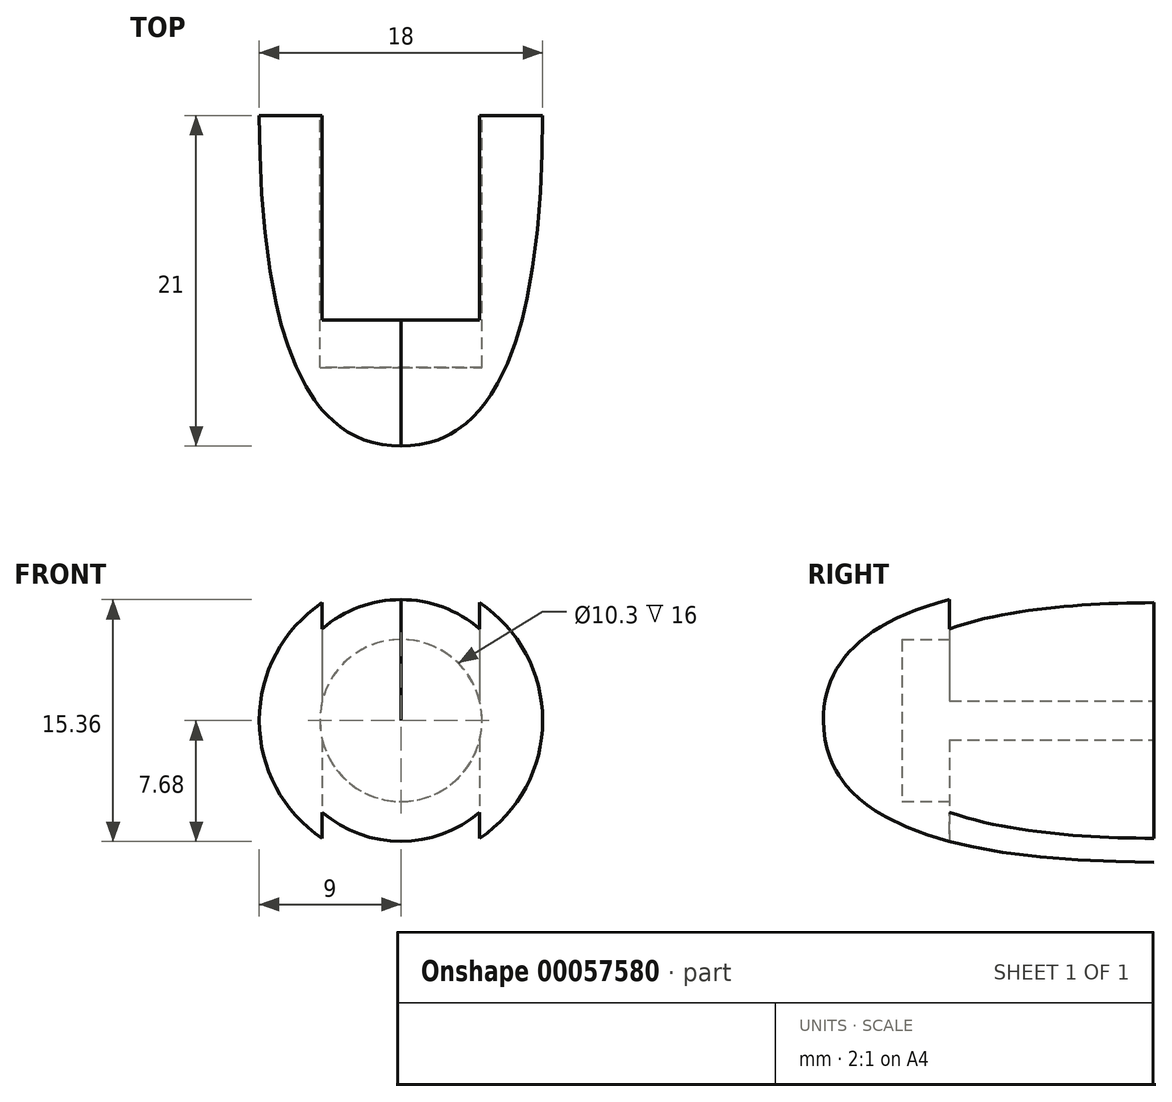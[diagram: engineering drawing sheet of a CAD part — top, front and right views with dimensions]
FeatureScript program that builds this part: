
annotation { "Feature Type Name" : "Feature", "Feature Type Description" : "" }
export const myFeature = defineFeature(function(context is Context, id is Id, definition is map)
    precondition{}
    {
        {
            var Q0;
            Q0=qCreatedBy(makeId("Right.planeOp"),FACE);
            var sketch = newSketch(context, id + "F0", { "sketchPlane" : qUnion([Q0])});
            skLineSegment(sketch, "E0", {"start": v(0, 0) * mm, "end": v(0, 5.15) * mm});
            skLineSegment(sketch, "E1", {"start": v(0, 5.15) * mm, "end": v(-16, 5.15) * mm});
            skLineSegment(sketch, "E2", {"start": v(-16, 5.15) * mm, "end": v(-16, 0) * mm});
            skLineSegment(sketch, "E3", {"start": v(-16, 0) * mm, "end": v(-21, 0) * mm});
            skFitSpline(sketch, "E4", {"points": [v(-21, 0) * mm, v(0, 9) * mm], "startDerivative": vector(0, 15.45) * mm, "endDerivative": vector(48, 0.13) * mm});
            skLineSegment(sketch, "E5", {"start": v(0, 9) * mm, "end": v(0, 5.15) * mm});
            skSolve(sketch);
        }
        {
            var Q0;
            Q0=makeQuery(id+"F0.imprint","IMPRINT",FACE,{"disambiguationData":[TD([[makeQuery(id+"F0.imprint","IMPRINT",EDGE,{"derivedFrom":sQuery(id+"F0.wireOp",EDGE,"E1")}),-1.0]])]});
            var Q1;
            Q1=sQuery(id+"F0.wireOp",EDGE,"E3");
            revolve(context, id + "F1", {"entities" : qUnion([Q0]), "axis" : qUnion([Q1]), "revolveType" : RevolveType.FULL});
        }
        {
            var Q0;
            Q0=makeQuery(id+"F1.opRevolve","SWEPT_FACE",FACE,{"disambiguationData":[OSD([sQuery(id+"F0.wireOp",EDGE,"E5")])]});
            var sketch = newSketch(context, id + "F2", { "sketchPlane" : qUnion([Q0])});
            skLineSegment(sketch, "E6.bottom", {"start": v(-5, 9) * mm, "end": v(5, 9) * mm});
            skLineSegment(sketch, "E6.left", {"start": v(-5, 9) * mm, "end": v(-5, -9) * mm});
            skLineSegment(sketch, "E6.right", {"start": v(5, 9) * mm, "end": v(5, -9) * mm});
            skLineSegment(sketch, "E7", {"start": v(-5, -9) * mm, "end": v(5, -9) * mm});
            skSolve(sketch);
        }
        {
            var Q0;
            Q0 = qSketchRegion(id + "F2", true);
            extrude(context, id + "F3", {"entities" : qUnion([Q0]), "operationType" : NewBodyOperationType.REMOVE, "oppositeDirection" : true, "depth" : 13 * mm});
        }
    });
